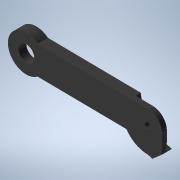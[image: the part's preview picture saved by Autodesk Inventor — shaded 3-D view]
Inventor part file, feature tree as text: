
AUTODESK INVENTOR PART (.ipt)
format: ipt  version: 2020.2 (Build 242310000, 310)  size: 249,344 bytes
history: native  units: mm
features: extrude x10, sketch x7, other x6, hole x2, projected_geometry x1
ambient origin geometry x8: Origin, YZ Plane, XZ Plane, XY Plane, X Axis, Y Axis, Z Axis, Center Point
bodies: Body1 (feature_tree)
feature tree (26):
  other  "ソリッド1"
  sketch  "スケッチ1"
  extrude  "押し出し1"  Depth=5.0mm
  extrude  "押し出し2"  Depth=6.0mm
  hole  "穴1"  [1 undecoded]
  extrude  "押し出し3"  Depth=17.771543mm
  extrude  "押し出し4"  Depth=0.5mm
  hole  "穴2"  [1 undecoded]
  sketch  "スケッチ4"
  extrude  "押し出し5"  Depth=2.75mm TaperAngle=0.0deg
  extrude  "押し出し6"  Depth=5.0mm
  sketch  "スケッチ6"
  extrude  "押し出し8"  Depth=5.0mm TaperAngle=0.0deg
  extrude  "押し出し9"  Depth=10.0mm TaperAngle=0.0deg
  extrude  "押し出し10"  Depth=15.0mm
  extrude  "押し出し11"  Depth=1.5mm
  sketch  "スケッチ2"
  sketch  "スケッチ3"
  projected_geometry  "投影ループ1"
  sketch  "スケッチ7"
  sketch  "スケッチ8"
  other  "断面エッジを投影1"
  other  "断面エッジを投影2"
  other  "断面エッジを投影3"
  other  "断面エッジを投影5"
  other  "断面エッジを投影6"
note: 2 required parameter values undecoded (feature->parameter linkage not recoverable at this tier; creation-order binding heuristic only, values carry confidence <= 0.55)
